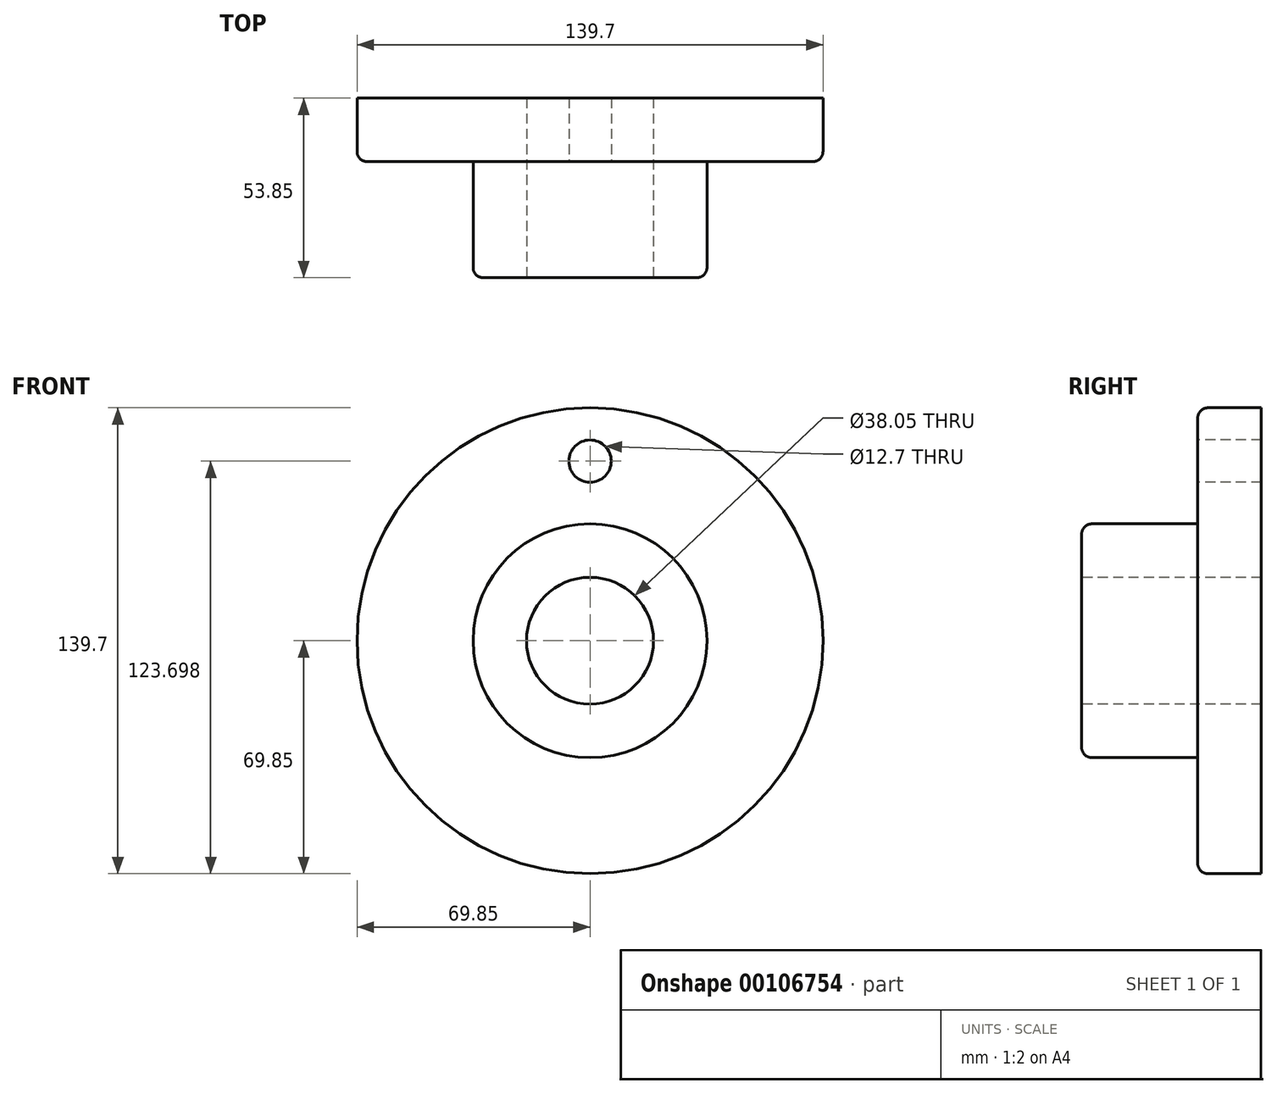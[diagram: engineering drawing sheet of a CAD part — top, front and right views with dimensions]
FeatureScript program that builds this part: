
annotation { "Feature Type Name" : "Feature", "Feature Type Description" : "" }
export const myFeature = defineFeature(function(context is Context, id is Id, definition is map)
    precondition{}
    {
        {
            var Q0;
            Q0=qCreatedBy(makeId("Front.planeOp"),FACE);
            var sketch = newSketch(context, id + "F0", { "sketchPlane" : qUnion([Q0])});
            skCircle(sketch, "E0", {"center": v(0, 0) * mm, "radius": 69.85 * mm});
            skSolve(sketch);
        }
        {
            var Q0;
            Q0 = qSketchRegion(id + "F0", true);
            extrude(context, id + "F1", {"entities" : qUnion([Q0]), "oppositeDirection" : true, "depth" : 19.05 * mm});
        }
        {
            var Q0;
            Q0=makeQuery(id+"F1.opExtrude","CAP_FACE",FACE,{"disambiguationData":[OSD([sQuery(id+"F0.wireOp",EDGE,"E0")])],"isStart":true});
            var sketch = newSketch(context, id + "F2", { "sketchPlane" : qUnion([Q0])});
            skCircle(sketch, "E1", {"center": v(0, 0) * mm, "radius": 35.05 * mm});
            skSolve(sketch);
        }
        {
            var Q0;
            Q0=makeQuery(id+"F2.imprint","IMPRINT",FACE,{"disambiguationData":[TD([[makeQuery(id+"F2.imprint","IMPRINT",EDGE,{"derivedFrom":sQuery(id+"F2.wireOp",EDGE,"E1")}),1.0]])]});
            extrude(context, id + "F3", {"entities" : qUnion([Q0]), "operationType" : NewBodyOperationType.ADD, "depth" : 34.8 * mm});
        }
        {
            var Q0;
            Q0=makeQuery(id+"F3.opExtrude","CAP_FACE",FACE,{"disambiguationData":[OSD([sQuery(id+"F2.wireOp",EDGE,"E1")])],"isStart":false});
            var sketch = newSketch(context, id + "F4", { "sketchPlane" : qUnion([Q0])});
            skCircle(sketch, "E2", {"center": v(0, 0) * mm, "radius": 19.02 * mm});
            skSolve(sketch);
        }
        {
            var Q0;
            Q0=makeQuery(id+"F4.imprint","IMPRINT",FACE,{"disambiguationData":[TD([[makeQuery(id+"F4.imprint","IMPRINT",EDGE,{"derivedFrom":sQuery(id+"F4.wireOp",EDGE,"E2")}),1.0]])]});
            extrude(context, id + "F5", {"entities" : qUnion([Q0]), "operationType" : NewBodyOperationType.REMOVE, "endBound" : BoundingType.THROUGH_ALL, "oppositeDirection" : true, "depth" : 25.4 * mm});
        }
        {
            var Q0;
            Q0=makeQuery(id+"F1.opExtrude","CAP_FACE",FACE,{"disambiguationData":[OSD([sQuery(id+"F0.wireOp",EDGE,"E0")])],"isStart":true});
            var sketch = newSketch(context, id + "F6", { "sketchPlane" : qUnion([Q0])});
            skCircle(sketch, "E3", {"center": v(0, 0) * mm, "radius": 53.85 * mm, "construction": true});
            skCircle(sketch, "E4", {"center": v(0, 53.85) * mm, "radius": 6.35 * mm});
            skSolve(sketch);
        }
        {
            var Q0;
            Q0=makeQuery(id+"F6.imprint","IMPRINT",FACE,{"disambiguationData":[TD([[makeQuery(id+"F6.imprint","IMPRINT",EDGE,{"derivedFrom":sQuery(id+"F6.wireOp",EDGE,"E4")}),1.0]])]});
            extrude(context, id + "F7", {"entities" : qUnion([Q0]), "operationType" : NewBodyOperationType.REMOVE, "endBound" : BoundingType.THROUGH_ALL, "oppositeDirection" : true, "depth" : 25.4 * mm});
        }
        {
            var Q0;
            Q0=makeQuery(id+"F3.opExtrude","CAP_EDGE",EDGE,{"disambiguationData":[OSD([sQuery(id+"F2.wireOp",EDGE,"E1")])],"isStart":false});
            var Q1;
            Q1=makeQuery(id+"F3.opExtrude","CAP_EDGE",EDGE,{"disambiguationData":[OSD([sQuery(id+"F2.wireOp",EDGE,"E1")])],"isStart":true});
            var Q2;
            Q2=makeQuery(id+"F1.opExtrude","CAP_EDGE",EDGE,{"disambiguationData":[OSD([sQuery(id+"F0.wireOp",EDGE,"E0")])],"isStart":true});
            fillet(context, id + "F8", {"entities" : qUnion([Q0, Q1, Q2]), "radius" : 3.05 * mm, "tangentPropagation" : true, "allowEdgeOverflow" : false});
        }
    });
